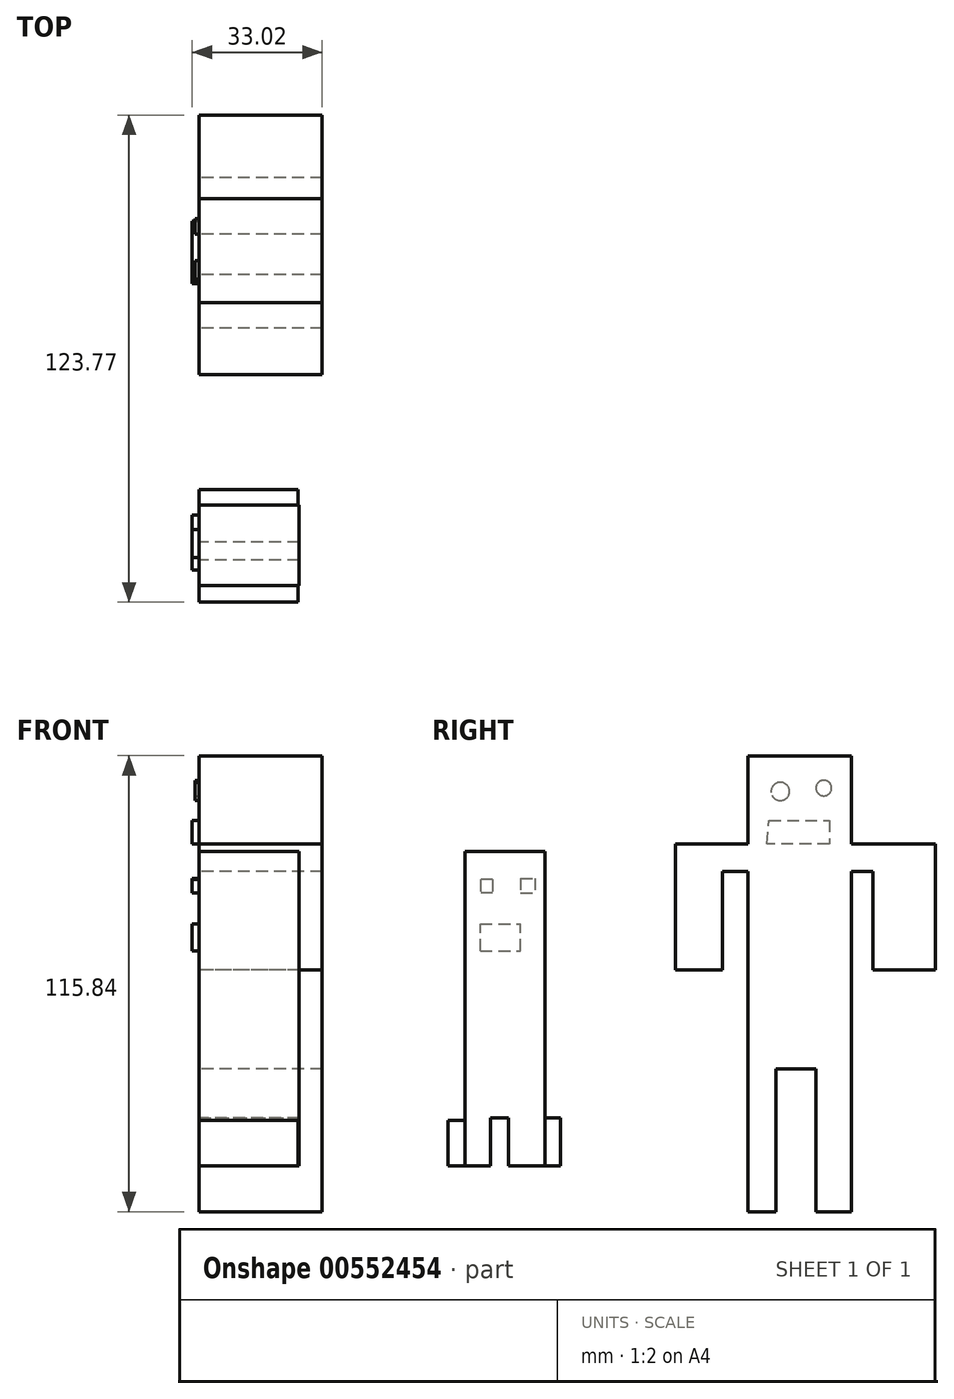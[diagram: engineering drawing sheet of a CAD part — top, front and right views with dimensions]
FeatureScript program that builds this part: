
annotation { "Feature Type Name" : "Feature", "Feature Type Description" : "" }
export const myFeature = defineFeature(function(context is Context, id is Id, definition is map)
    precondition{}
    {
        {
            var Q0;
            Q0=qCreatedBy(makeId("Right.planeOp"),FACE);
            var sketch = newSketch(context, id + "F0", { "sketchPlane" : qUnion([Q0])});
            skLineSegment(sketch, "E0.bottom", {"start": v(30.3, 67.27) * mm, "end": v(3.97, 67.27) * mm});
            skLineSegment(sketch, "E0.top", {"start": v(30.3, 44.9) * mm, "end": v(3.97, 44.9) * mm});
            skLineSegment(sketch, "E0.left", {"start": v(30.3, 67.27) * mm, "end": v(30.3, 44.9) * mm});
            skLineSegment(sketch, "E0.right", {"start": v(3.97, 67.27) * mm, "end": v(3.97, 44.9) * mm});
            skLineSegment(sketch, "E1.bottom", {"start": v(3.97, 44.9) * mm, "end": v(30.3, 44.9) * mm});
            skLineSegment(sketch, "E1.top", {"start": v(3.97, -12.32) * mm, "end": v(30.3, -12.32) * mm});
            skLineSegment(sketch, "E1.left", {"start": v(3.97, 44.9) * mm, "end": v(3.97, -12.32) * mm});
            skLineSegment(sketch, "E1.right", {"start": v(30.3, 44.9) * mm, "end": v(30.3, -12.32) * mm});
            skLineSegment(sketch, "E2.bottom", {"start": v(30.3, 44.9) * mm, "end": v(35.69, 44.9) * mm});
            skLineSegment(sketch, "E2.top", {"start": v(30.3, 37.81) * mm, "end": v(35.69, 37.81) * mm});
            skLineSegment(sketch, "E2.left", {"start": v(30.3, 44.9) * mm, "end": v(30.3, 37.81) * mm});
            skLineSegment(sketch, "E2.right", {"start": v(35.69, 44.9) * mm, "end": v(35.69, 37.81) * mm});
            skLineSegment(sketch, "E3.bottom", {"start": v(35.69, 44.9) * mm, "end": v(51.55, 44.9) * mm});
            skLineSegment(sketch, "E3.top", {"start": v(35.69, 12.89) * mm, "end": v(51.55, 12.89) * mm});
            skLineSegment(sketch, "E3.left", {"start": v(35.69, 44.9) * mm, "end": v(35.69, 12.89) * mm});
            skLineSegment(sketch, "E3.right", {"start": v(51.55, 44.9) * mm, "end": v(51.55, 12.89) * mm});
            skLineSegment(sketch, "E4.bottom", {"start": v(3.97, 44.9) * mm, "end": v(-2.55, 44.9) * mm});
            skLineSegment(sketch, "E4.top", {"start": v(3.97, 37.81) * mm, "end": v(-2.55, 37.81) * mm});
            skLineSegment(sketch, "E4.left", {"start": v(3.97, 44.9) * mm, "end": v(3.97, 37.81) * mm});
            skLineSegment(sketch, "E4.right", {"start": v(-2.55, 44.9) * mm, "end": v(-2.55, 37.81) * mm});
            skLineSegment(sketch, "E5.bottom", {"start": v(-2.55, 44.9) * mm, "end": v(-14.44, 44.9) * mm});
            skLineSegment(sketch, "E5.top", {"start": v(-2.55, 12.89) * mm, "end": v(-14.44, 12.89) * mm});
            skLineSegment(sketch, "E5.left", {"start": v(-2.55, 44.9) * mm, "end": v(-2.55, 12.89) * mm});
            skLineSegment(sketch, "E5.right", {"start": v(-14.44, 44.9) * mm, "end": v(-14.44, 12.89) * mm});
            skLineSegment(sketch, "E6.bottom", {"start": v(21.24, -12.32) * mm, "end": v(30.3, -12.32) * mm});
            skLineSegment(sketch, "E6.top", {"start": v(21.24, -48.57) * mm, "end": v(30.3, -48.57) * mm});
            skLineSegment(sketch, "E6.left", {"start": v(21.24, -12.32) * mm, "end": v(21.24, -48.57) * mm});
            skLineSegment(sketch, "E6.right", {"start": v(30.3, -12.32) * mm, "end": v(30.3, -48.57) * mm});
            skLineSegment(sketch, "E7.bottom", {"start": v(3.97, -12.32) * mm, "end": v(11.05, -12.32) * mm});
            skLineSegment(sketch, "E7.top", {"start": v(3.97, -48.57) * mm, "end": v(11.05, -48.57) * mm});
            skLineSegment(sketch, "E7.left", {"start": v(3.97, -12.32) * mm, "end": v(3.97, -48.57) * mm});
            skLineSegment(sketch, "E7.right", {"start": v(11.05, -12.32) * mm, "end": v(11.05, -48.57) * mm});
            skSolve(sketch);
        }
        {
            var Q0;
            Q0 = qSketchRegion(id + "F0", true);
            extrude(context, id + "F1", {"entities" : qUnion([Q0]), "depth" : 31.24 * mm, "offsetDistance" : 25.4 * mm});
        }
        {
            var Q0;
            Q0=makeQuery(id+"F1.opExtrude","CAP_FACE",FACE,{"disambiguationData":[OSD([sQuery(id+"F0.wireOp",EDGE,"E0.bottom"),sQuery(id+"F0.wireOp",EDGE,"E0.left"),sQuery(id+"F0.wireOp",EDGE,"E0.right"),sQuery(id+"F0.wireOp",EDGE,"E1.top"),sQuery(id+"F0.wireOp",EDGE,"E1.left"),sQuery(id+"F0.wireOp",EDGE,"E1.right"),sQuery(id+"F0.wireOp",EDGE,"E2.bottom"),sQuery(id+"F0.wireOp",EDGE,"E2.top"),sQuery(id+"F0.wireOp",EDGE,"E3.bottom"),sQuery(id+"F0.wireOp",EDGE,"E3.top"),sQuery(id+"F0.wireOp",EDGE,"E3.left"),sQuery(id+"F0.wireOp",EDGE,"E3.right"),sQuery(id+"F0.wireOp",EDGE,"E4.bottom"),sQuery(id+"F0.wireOp",EDGE,"E4.top"),sQuery(id+"F0.wireOp",EDGE,"E5.bottom"),sQuery(id+"F0.wireOp",EDGE,"E5.top"),sQuery(id+"F0.wireOp",EDGE,"E5.left"),sQuery(id+"F0.wireOp",EDGE,"E5.right"),sQuery(id+"F0.wireOp",EDGE,"E6.top"),sQuery(id+"F0.wireOp",EDGE,"E6.left"),sQuery(id+"F0.wireOp",EDGE,"E6.right"),sQuery(id+"F0.wireOp",EDGE,"E7.top"),sQuery(id+"F0.wireOp",EDGE,"E7.left"),sQuery(id+"F0.wireOp",EDGE,"E7.right")])],"isStart":true});
            var sketch = newSketch(context, id + "F2", { "sketchPlane" : qUnion([Q0])});
            skCircle(sketch, "E8", {"center": v(-23.22, 59.05) * mm, "radius": 1.98 * mm});
            skCircle(sketch, "E9", {"center": v(-12.18, 58.2) * mm, "radius": 2.34 * mm});
            skLineSegment(sketch, "E10", {"start": v(-9.35, 50.84) * mm, "end": v(-24.64, 50.84) * mm});
            skLineSegment(sketch, "E11", {"start": v(-24.64, 50.84) * mm, "end": v(-24.64, 44.9) * mm});
            skLineSegment(sketch, "E12", {"start": v(-24.64, 44.9) * mm, "end": v(-8.78, 44.9) * mm});
            skLineSegment(sketch, "E13", {"start": v(-8.78, 44.9) * mm, "end": v(-9.35, 50.84) * mm});
            skSolve(sketch);
        }
        {
            var Q0;
            Q0=makeQuery(id+"F2.imprint","IMPRINT",FACE,{"disambiguationData":[TD([[makeQuery(id+"F2.imprint","IMPRINT",EDGE,{"derivedFrom":sQuery(id+"F2.wireOp",EDGE,"E10")}),1.0]])]});
            extrude(context, id + "F3", {"entities" : qUnion([Q0]), "operationType" : NewBodyOperationType.ADD, "depth" : 1.78 * mm, "offsetDistance" : 25.4 * mm});
        }
        {
            var Q0;
            Q0 = qSketchRegion(id + "F2", true);
            extrude(context, id + "F4", {"entities" : qUnion([Q0]), "operationType" : NewBodyOperationType.ADD, "depth" : 1.02 * mm, "offsetDistance" : 25.4 * mm});
        }
        {
            var Q0;
            Q0=qCreatedBy(makeId("Right.planeOp"),FACE);
            var sketch = newSketch(context, id + "F5", { "sketchPlane" : qUnion([Q0])});
            skLineSegment(sketch, "E14.bottom", {"start": v(-67.97, 42.9) * mm, "end": v(-47.58, 42.9) * mm});
            skLineSegment(sketch, "E14.top", {"start": v(-67.97, 21.95) * mm, "end": v(-47.58, 21.95) * mm});
            skLineSegment(sketch, "E14.left", {"start": v(-67.97, 42.9) * mm, "end": v(-67.97, 21.95) * mm});
            skLineSegment(sketch, "E14.right", {"start": v(-47.58, 42.9) * mm, "end": v(-47.58, 21.95) * mm});
            skLineSegment(sketch, "E15.top", {"start": v(-67.97, -24.78) * mm, "end": v(-47.58, -24.78) * mm});
            skLineSegment(sketch, "E15.left", {"start": v(-67.97, 21.95) * mm, "end": v(-67.97, -24.78) * mm});
            skLineSegment(sketch, "E15.right", {"start": v(-47.58, 21.95) * mm, "end": v(-47.58, -24.78) * mm});
            skLineSegment(sketch, "E16.bottom", {"start": v(-47.58, -24.78) * mm, "end": v(-56.93, -24.78) * mm});
            skLineSegment(sketch, "E16.top", {"start": v(-47.58, -36.96) * mm, "end": v(-56.93, -36.96) * mm});
            skLineSegment(sketch, "E16.left", {"start": v(-47.58, -24.78) * mm, "end": v(-47.58, -36.96) * mm});
            skLineSegment(sketch, "E16.right", {"start": v(-56.93, -24.78) * mm, "end": v(-56.93, -36.96) * mm});
            skLineSegment(sketch, "E17.bottom", {"start": v(-67.97, -24.78) * mm, "end": v(-61.46, -24.78) * mm});
            skLineSegment(sketch, "E17.top", {"start": v(-67.97, -34.7) * mm, "end": v(-61.46, -34.7) * mm});
            skLineSegment(sketch, "E17.left", {"start": v(-67.97, -24.78) * mm, "end": v(-67.97, -34.7) * mm});
            skLineSegment(sketch, "E17.right", {"start": v(-61.46, -24.78) * mm, "end": v(-61.46, -34.7) * mm});
            skLineSegment(sketch, "E18.top", {"start": v(-67.97, -36.96) * mm, "end": v(-61.46, -36.96) * mm});
            skLineSegment(sketch, "E18.left", {"start": v(-67.97, -34.7) * mm, "end": v(-67.97, -36.96) * mm});
            skLineSegment(sketch, "E18.right", {"start": v(-61.46, -34.7) * mm, "end": v(-61.46, -36.96) * mm});
            skSolve(sketch);
        }
        {
            var Q0;
            Q0 = qSketchRegion(id + "F5", true);
            extrude(context, id + "F6", {"entities" : qUnion([Q0]), "depth" : 25.4 * mm, "offsetDistance" : 25.4 * mm});
        }
        {
            var Q0;
            Q0=makeQuery(id+"F6.opExtrude","CAP_FACE",FACE,{"disambiguationData":[OSD([sQuery(id+"F5.wireOp",EDGE,"E14.bottom"),sQuery(id+"F5.wireOp",EDGE,"E14.left"),sQuery(id+"F5.wireOp",EDGE,"E14.right"),sQuery(id+"F5.wireOp",EDGE,"E15.top"),sQuery(id+"F5.wireOp",EDGE,"E15.left"),sQuery(id+"F5.wireOp",EDGE,"E15.right"),sQuery(id+"F5.wireOp",EDGE,"E16.top"),sQuery(id+"F5.wireOp",EDGE,"E16.left"),sQuery(id+"F5.wireOp",EDGE,"E16.right"),sQuery(id+"F5.wireOp",EDGE,"E17.left"),sQuery(id+"F5.wireOp",EDGE,"E17.right"),sQuery(id+"F5.wireOp",EDGE,"E18.top"),sQuery(id+"F5.wireOp",EDGE,"E18.left"),sQuery(id+"F5.wireOp",EDGE,"E18.right")])],"isStart":true});
            var sketch = newSketch(context, id + "F7", { "sketchPlane" : qUnion([Q0])});
            skLineSegment(sketch, "E19.bottom", {"start": v(67.97, -25.35) * mm, "end": v(72.22, -25.35) * mm});
            skLineSegment(sketch, "E19.top", {"start": v(67.97, -36.96) * mm, "end": v(72.22, -36.96) * mm});
            skLineSegment(sketch, "E19.left", {"start": v(67.97, -25.35) * mm, "end": v(67.97, -36.96) * mm});
            skLineSegment(sketch, "E19.right", {"start": v(72.22, -25.35) * mm, "end": v(72.22, -36.96) * mm});
            skLineSegment(sketch, "E20.bottom", {"start": v(47.58, -36.96) * mm, "end": v(56.93, -36.96) * mm});
            skLineSegment(sketch, "E20.top", {"start": v(47.58, -24.78) * mm, "end": v(56.93, -24.78) * mm});
            skLineSegment(sketch, "E20.left", {"start": v(47.58, -36.96) * mm, "end": v(47.58, -24.78) * mm});
            skLineSegment(sketch, "E20.right", {"start": v(56.93, -36.96) * mm, "end": v(56.93, -24.78) * mm});
            skLineSegment(sketch, "E21.bottom", {"start": v(47.58, -24.78) * mm, "end": v(43.62, -24.78) * mm});
            skLineSegment(sketch, "E21.top", {"start": v(47.58, -36.96) * mm, "end": v(43.62, -36.96) * mm});
            skLineSegment(sketch, "E21.left", {"start": v(47.58, -24.78) * mm, "end": v(47.58, -36.96) * mm});
            skLineSegment(sketch, "E21.right", {"start": v(43.62, -24.78) * mm, "end": v(43.62, -36.96) * mm});
            skSolve(sketch);
        }
        {
            var Q0;
            Q0 = qSketchRegion(id + "F7", true);
            extrude(context, id + "F8", {"entities" : qUnion([Q0]), "operationType" : NewBodyOperationType.ADD, "oppositeDirection" : true, "depth" : 25.15 * mm, "offsetDistance" : 25.4 * mm});
        }
        {
            var Q0;
            Q0=makeQuery(id+"F8.boolean.opBoolean","MERGE",FACE,{"derivedFrom":[makeQuery(id+"F6.opExtrude","CAP_FACE",FACE,{"disambiguationData":[OSD([sQuery(id+"F5.wireOp",EDGE,"E14.bottom"),sQuery(id+"F5.wireOp",EDGE,"E14.left"),sQuery(id+"F5.wireOp",EDGE,"E14.right"),sQuery(id+"F5.wireOp",EDGE,"E15.top"),sQuery(id+"F5.wireOp",EDGE,"E15.left"),sQuery(id+"F5.wireOp",EDGE,"E15.right"),sQuery(id+"F5.wireOp",EDGE,"E16.top"),sQuery(id+"F5.wireOp",EDGE,"E16.left"),sQuery(id+"F5.wireOp",EDGE,"E16.right"),sQuery(id+"F5.wireOp",EDGE,"E17.left"),sQuery(id+"F5.wireOp",EDGE,"E17.right"),sQuery(id+"F5.wireOp",EDGE,"E18.top"),sQuery(id+"F5.wireOp",EDGE,"E18.left"),sQuery(id+"F5.wireOp",EDGE,"E18.right")])],"isStart":true}),makeQuery(id+"F8.opExtrude","CAP_FACE",FACE,{"disambiguationData":[OSD([sQuery(id+"F7.wireOp",EDGE,"E19.bottom"),sQuery(id+"F7.wireOp",EDGE,"E19.top"),sQuery(id+"F7.wireOp",EDGE,"E19.left"),sQuery(id+"F7.wireOp",EDGE,"E19.right")])],"isStart":true}),makeQuery(id+"F8.opExtrude","CAP_FACE",FACE,{"disambiguationData":[OSD([sQuery(id+"F7.wireOp",EDGE,"E20.bottom"),sQuery(id+"F7.wireOp",EDGE,"E20.top"),sQuery(id+"F7.wireOp",EDGE,"E20.right"),sQuery(id+"F7.wireOp",EDGE,"E21.bottom"),sQuery(id+"F7.wireOp",EDGE,"E21.top"),sQuery(id+"F7.wireOp",EDGE,"E21.right")])],"isStart":true})]});
            var sketch = newSketch(context, id + "F9", { "sketchPlane" : qUnion([Q0])});
            skLineSegment(sketch, "E22.bottom", {"start": v(53.81, 36.11) * mm, "end": v(50.13, 36.11) * mm});
            skLineSegment(sketch, "E22.top", {"start": v(53.81, 32.43) * mm, "end": v(50.13, 32.43) * mm});
            skLineSegment(sketch, "E22.left", {"start": v(53.81, 36.11) * mm, "end": v(53.81, 32.43) * mm});
            skLineSegment(sketch, "E22.right", {"start": v(50.13, 36.11) * mm, "end": v(50.13, 32.43) * mm});
            skLineSegment(sketch, "E23.bottom", {"start": v(60.9, 35.83) * mm, "end": v(64, 35.83) * mm});
            skLineSegment(sketch, "E23.top", {"start": v(60.9, 32.43) * mm, "end": v(64, 32.43) * mm});
            skLineSegment(sketch, "E23.left", {"start": v(60.9, 35.83) * mm, "end": v(60.9, 32.43) * mm});
            skLineSegment(sketch, "E23.right", {"start": v(64, 35.83) * mm, "end": v(64, 32.43) * mm});
            skLineSegment(sketch, "E24.bottom", {"start": v(64, 24.5) * mm, "end": v(53.81, 24.5) * mm});
            skLineSegment(sketch, "E24.top", {"start": v(64, 20.82) * mm, "end": v(53.81, 20.82) * mm});
            skLineSegment(sketch, "E24.left", {"start": v(64, 24.5) * mm, "end": v(64, 20.82) * mm});
            skLineSegment(sketch, "E24.right", {"start": v(53.81, 24.5) * mm, "end": v(53.81, 20.82) * mm});
            skPoint(sketch, "E25.oppositeSnap0", {"position": v(58.91, 20.82) * mm});
            skLineSegment(sketch, "E25.bottom", {"start": v(60.9, 20.82) * mm, "end": v(58.91, 20.82) * mm});
            skLineSegment(sketch, "E25.top", {"start": v(60.9, 17.7) * mm, "end": v(58.91, 17.7) * mm});
            skLineSegment(sketch, "E25.left", {"start": v(60.9, 20.82) * mm, "end": v(60.9, 17.7) * mm});
            skLineSegment(sketch, "E25.right", {"start": v(58.91, 20.82) * mm, "end": v(58.91, 17.7) * mm});
            skLineSegment(sketch, "E26.bottom", {"start": v(58.91, 17.7) * mm, "end": v(53.81, 17.7) * mm});
            skLineSegment(sketch, "E26.top", {"start": v(58.91, 20.82) * mm, "end": v(53.81, 20.82) * mm});
            skLineSegment(sketch, "E26.left", {"start": v(58.91, 17.7) * mm, "end": v(58.91, 20.82) * mm});
            skLineSegment(sketch, "E26.right", {"start": v(53.81, 17.7) * mm, "end": v(53.81, 20.82) * mm});
            skLineSegment(sketch, "E27.bottom", {"start": v(60.9, 17.7) * mm, "end": v(64, 17.7) * mm});
            skLineSegment(sketch, "E27.top", {"start": v(60.9, 20.82) * mm, "end": v(64, 20.82) * mm});
            skLineSegment(sketch, "E27.left", {"start": v(60.9, 17.7) * mm, "end": v(60.9, 20.82) * mm});
            skLineSegment(sketch, "E27.right", {"start": v(64, 17.7) * mm, "end": v(64, 20.82) * mm});
            skSolve(sketch);
        }
        {
            var Q0;
            Q0 = qSketchRegion(id + "F9", true);
            extrude(context, id + "F10", {"entities" : qUnion([Q0]), "operationType" : NewBodyOperationType.ADD, "depth" : 1.78 * mm, "offsetDistance" : 25.4 * mm});
        }
    });
